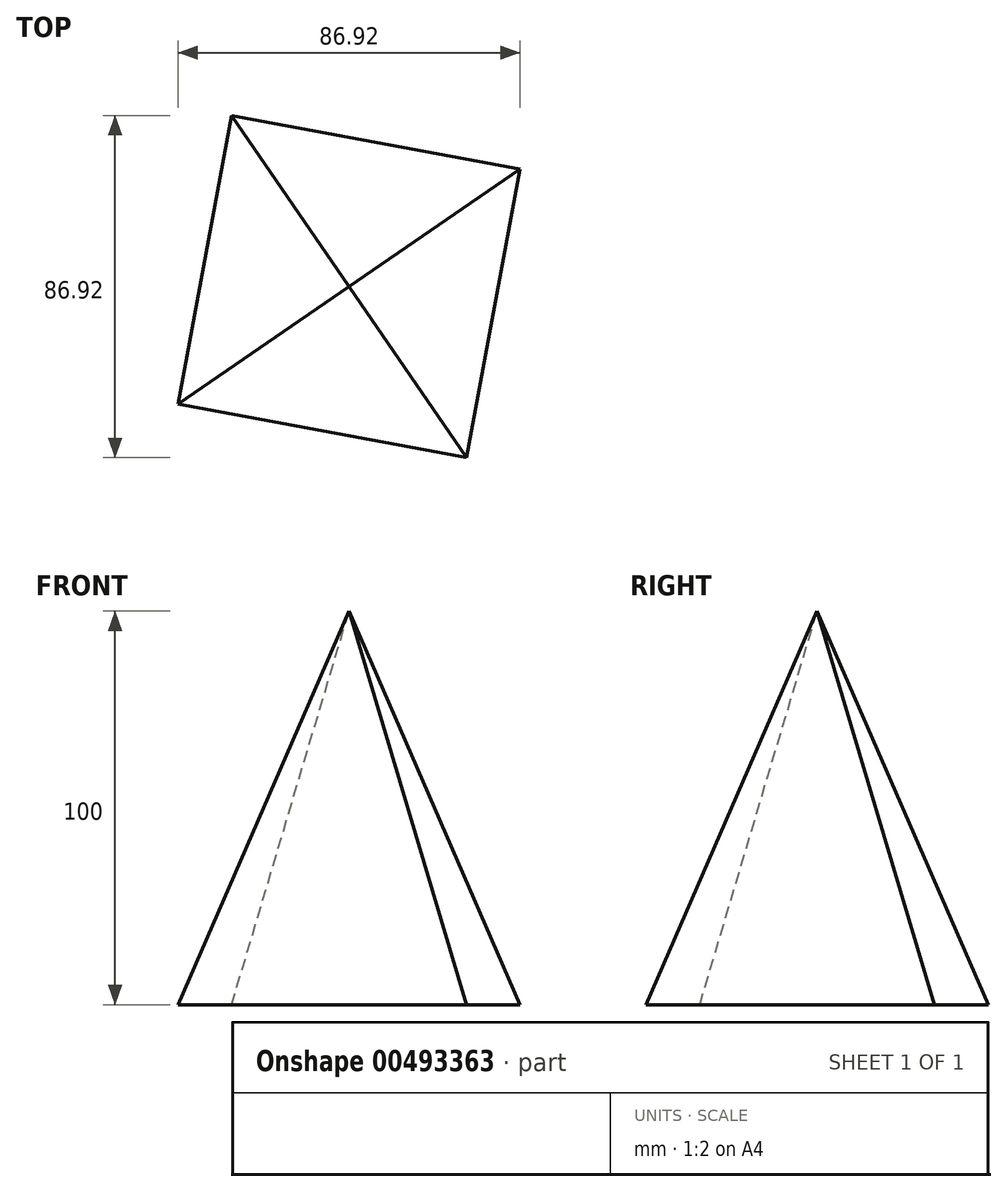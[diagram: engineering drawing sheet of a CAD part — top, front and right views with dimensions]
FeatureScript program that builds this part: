
annotation { "Feature Type Name" : "Feature", "Feature Type Description" : "" }
export const myFeature = defineFeature(function(context is Context, id is Id, definition is map)
    precondition{}
    {
        {
            var Q0;
            Q0=qCreatedBy(makeId("Top.planeOp"),FACE);
            var sketch = newSketch(context, id + "F0", { "sketchPlane" : qUnion([Q0])});
            skCircle(sketch, "E0.cCircle", {"center": v(0, 0) * mm, "radius": 52.72 * mm, "construction": true});
            skLineSegment(sketch, "E0.0", {"start": v(-29.84, 43.46) * mm, "end": v(43.46, 29.84) * mm});
            skLineSegment(sketch, "E0.1", {"start": v(43.46, 29.84) * mm, "end": v(29.84, -43.46) * mm});
            skLineSegment(sketch, "E0.2", {"start": v(29.84, -43.46) * mm, "end": v(-43.46, -29.84) * mm});
            skLineSegment(sketch, "E0.3", {"start": v(-43.46, -29.84) * mm, "end": v(-29.84, 43.46) * mm});
            skSolve(sketch);
        }
        {
            var Q0;
            Q0=qCreatedBy(makeId("Top.planeOp"),FACE);
            cPlane(context, id + "F1", {"entities" : qUnion([Q0]), "cplaneType" : CPlaneType.OFFSET, "offset" : 100 * mm, "width" : 150 * mm, "height" : 150 * mm});
        }
        {
            var Q0;
            Q0=qCreatedBy(id+"F1.planeOp",FACE);
            var sketch = newSketch(context, id + "F2", { "sketchPlane" : qUnion([Q0])});
            skPoint(sketch, "E1", {"position": v(0, 0) * mm});
            skSolve(sketch);
        }
        {
            var Q0;
            Q0=makeQuery(id+"F0.imprint","IMPRINT",FACE,{"disambiguationData":[TD([[makeQuery(id+"F0.imprint","IMPRINT",EDGE,{"derivedFrom":sQuery(id+"F0.wireOp",EDGE,"E0.0")}),-1.0]])]});
            var Q1;
            Q1=sQuery(id+"F2.wireOp",VERTEX,"E1");
            loft(context, id + "F3", {"sheetProfilesArray" : [{ "sheetProfileEntities" : qUnion([Q0]) }, { "sheetProfileEntities" : qUnion([Q1]) }]});
        }
    });
